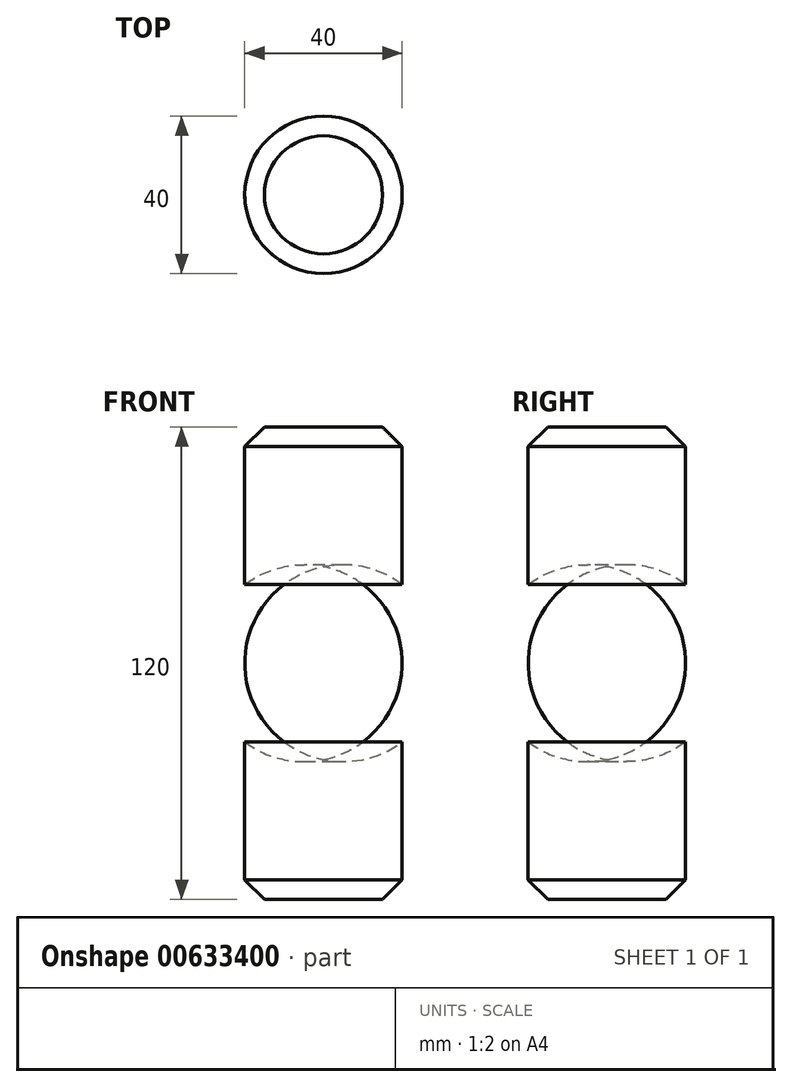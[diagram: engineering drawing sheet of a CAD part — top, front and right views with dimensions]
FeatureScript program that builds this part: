
annotation { "Feature Type Name" : "Feature", "Feature Type Description" : "" }
export const myFeature = defineFeature(function(context is Context, id is Id, definition is map)
    precondition{}
    {
        {
            var Q0;
            Q0=qCreatedBy(makeId("Front.planeOp"),FACE);
            var sketch = newSketch(context, id + "F0", { "sketchPlane" : qUnion([Q0])});
            skLineSegment(sketch, "E0", {"start": v(0, 60) * mm, "end": v(0, -60) * mm});
            skLineSegment(sketch, "E1", {"start": v(0, -60) * mm, "end": v(20, -60) * mm});
            skLineSegment(sketch, "E2", {"start": v(20, -60) * mm, "end": v(20, -20) * mm});
            skLineSegment(sketch, "E3", {"start": v(0, 60) * mm, "end": v(20, 60) * mm});
            skLineSegment(sketch, "E4", {"start": v(20, 60) * mm, "end": v(20, 20) * mm});
            skArc(sketch, "E5", {"start": v(20, -20) * mm, "mid": v(30, 0) * mm, "end": v(20, 20) * mm});
            skSolve(sketch);
        }
        {
            var Q0;
            Q0=makeQuery(id+"F0.imprint","IMPRINT",FACE,{"disambiguationData":[TD([[makeQuery(id+"F0.imprint","IMPRINT",EDGE,{"derivedFrom":sQuery(id+"F0.wireOp",EDGE,"E0")}),1.0]])]});
            var Q1;
            Q1=sQuery(id+"F0.wireOp",EDGE,"E0");
            revolve(context, id + "F1", {"entities" : qUnion([Q0]), "axis" : qUnion([Q1]), "revolveType" : RevolveType.FULL});
        }
        {
            var Q0;
            Q0=makeQuery(id+"F1.opRevolve","SWEPT_EDGE",EDGE,{"disambiguationData":[OSD([sQuery(id+"F0.wireOp",EDGE,"E3"),sQuery(id+"F0.wireOp",EDGE,"E4")])]});
            chamfer(context, id + "F2", {"entities" : qUnion([Q0]), "width" : 5 * mm, "tangentPropagation" : true});
        }
        {
            var Q0;
            Q0=makeQuery(id+"F1.opRevolve","SWEPT_EDGE",EDGE,{"disambiguationData":[OSD([sQuery(id+"F0.wireOp",EDGE,"E1"),sQuery(id+"F0.wireOp",EDGE,"E2")])]});
            chamfer(context, id + "F3", {"entities" : qUnion([Q0]), "width" : 5 * mm, "tangentPropagation" : true});
        }
        {
            var Q0;
            Q0=qCreatedBy(makeId("Front.planeOp"),FACE);
            cPlane(context, id + "F4", {"entities" : qUnion([Q0]), "cplaneType" : CPlaneType.OFFSET, "offset" : 25 * mm, "width" : 150 * mm, "height" : 150 * mm});
        }
        {
            var Q0;
            Q0=qCreatedBy(id+"F4.planeOp",FACE);
            var sketch = newSketch(context, id + "F5", { "sketchPlane" : qUnion([Q0])});
            skLineSegment(sketch, "E6.bottom", {"start": v(0, -10) * mm, "end": v(0, -10) * mm});
            skLineSegment(sketch, "E6.top", {"start": v(0, 10) * mm, "end": v(0, 10) * mm});
            skLineSegment(sketch, "E6.left", {"start": v(5, -5) * mm, "end": v(5, 5) * mm});
            skLineSegment(sketch, "E6.right", {"start": v(-5, -5) * mm, "end": v(-5, 5) * mm});
            skPoint(sketch, "E6.middle", {"position": v(0, 0) * mm});
            skPoint(sketch, "E7.visualSharp", {"position": v(-5, 10) * mm});
            skArc(sketch, "E7.filletArc", {"start": v(0, 10) * mm, "mid": v(-3.54, 8.54) * mm, "end": v(-5, 5) * mm});
            skPoint(sketch, "E8.visualSharp", {"position": v(5, 10) * mm});
            skArc(sketch, "E8.filletArc", {"start": v(5, 5) * mm, "mid": v(3.54, 8.54) * mm, "end": v(0, 10) * mm});
            skPoint(sketch, "E9.visualSharp", {"position": v(5, -10) * mm});
            skArc(sketch, "E9.filletArc", {"start": v(0, -10) * mm, "mid": v(3.54, -8.54) * mm, "end": v(5, -5) * mm});
            skPoint(sketch, "E10.visualSharp", {"position": v(-5, -10) * mm});
            skArc(sketch, "E10.filletArc", {"start": v(-5, -5) * mm, "mid": v(-3.54, -8.54) * mm, "end": v(0, -10) * mm});
            skSolve(sketch);
        }
        {
            var Q0;
            Q0=qCreatedBy(makeId("Right.planeOp"),FACE);
            var sketch = newSketch(context, id + "F6", { "sketchPlane" : qUnion([Q0])});
            skFitSpline(sketch, "E11", {"points": [v(-25, 0) * mm, v(-68.86, 35.46) * mm, v(-94.43, 26.77) * mm, v(-120.48, 33.53) * mm], "startDerivative": vector(-59.33, 123) * mm, "endDerivative": vector(-83.67, 41.82) * mm});
            skSolve(sketch);
        }
        {
            var Q0;
            Q0 = qSketchRegion(id + "F5", true);
            var Q1;
            Q1=sQuery(id+"F6.wireOp",EDGE,"E11");
            sweep(context, id + "F7", {"operationType" : NewBodyOperationType.ADD, "profiles" : qUnion([Q0]), "path" : qUnion([Q1])});
        }
        {
            var Q0;
            Q0=makeQuery(id+"F1.opRevolve","SWEPT_BODY",BODY,{"disambiguationData":[OSD([sQuery(id+"F0.wireOp",EDGE,"E0"),sQuery(id+"F0.wireOp",EDGE,"E1"),sQuery(id+"F0.wireOp",EDGE,"E2"),sQuery(id+"F0.wireOp",EDGE,"E3"),sQuery(id+"F0.wireOp",EDGE,"E4"),sQuery(id+"F0.wireOp",EDGE,"E5")])]});
            var Q1;
            Q1=makeQuery(id+"F1.opRevolve","SWEPT_FACE",FACE,{"disambiguationData":[OSD([sQuery(id+"F0.wireOp",EDGE,"E4")])]});
            circularPattern(context, id + "F8", {"entities" : qUnion([Q0]), "axis" : qUnion([Q1]), "angle" : 360 * degree, "instanceCount" : 5, "equalSpace" : true});
        }
        {
            var Q0;
            Q0=qCreatedBy(makeId("Front.planeOp"),FACE);
            var sketch = newSketch(context, id + "F9", { "sketchPlane" : qUnion([Q0])});
            skCircle(sketch, "E12", {"center": v(120, 30) * mm, "radius": 15 * mm});
            skSolve(sketch);
        }
        {
            var Q0;
            Q0 = qSketchRegion(id + "F9", true);
            var Q1;
            Q1=makeQuery(id+"F1.opRevolve","SWEPT_FACE",FACE,{"disambiguationData":[OSD([sQuery(id+"F0.wireOp",EDGE,"E4")])]});
            revolve(context, id + "F10", {"operationType" : NewBodyOperationType.ADD, "entities" : qUnion([Q0]), "axis" : qUnion([Q1]), "revolveType" : RevolveType.FULL});
        }
        {
            var Q0;
            Q0=makeQuery(id+"F10.boolean.opBoolean","INTERSECT",EDGE,{"derivedFrom":[makeQuery(id+"F8.opPattern","COPY",FACE,{"derivedFrom":makeQuery(id+"F7.opSweep","SWEPT_FACE",FACE,{"disambiguationData":[OSD([sQuery(id+"F5.wireOp",EDGE,"E6.left"),sQuery(id+"F6.wireOp",EDGE,"E11")])]}),"instanceName":"1"}),makeQuery(id+"F10.opRevolve","SWEPT_FACE",FACE,{"disambiguationData":[OSD([sQuery(id+"F9.wireOp",EDGE,"E12")])]})]});
            fillet(context, id + "F11", {"entities" : qUnion([Q0]), "radius" : 5 * mm, "tangentPropagation" : true, "allowEdgeOverflow" : false});
        }
        {
            var Q0;
            Q0=makeQuery(id+"F10.boolean.opBoolean","INTERSECT",EDGE,{"derivedFrom":[makeQuery(id+"F8.opPattern","COPY",FACE,{"derivedFrom":makeQuery(id+"F7.opSweep","SWEPT_FACE",FACE,{"disambiguationData":[OSD([sQuery(id+"F5.wireOp",EDGE,"E7.filletArc"),sQuery(id+"F5.wireOp",EDGE,"E8.filletArc"),sQuery(id+"F6.wireOp",EDGE,"E11")])]}),"instanceName":"2"}),makeQuery(id+"F10.opRevolve","SWEPT_FACE",FACE,{"disambiguationData":[OSD([sQuery(id+"F9.wireOp",EDGE,"E12")])]})]});
            var Q1;
            Q1=makeQuery(id+"F10.boolean.opBoolean","INTERSECT",EDGE,{"derivedFrom":[makeQuery(id+"F8.opPattern","COPY",FACE,{"derivedFrom":makeQuery(id+"F7.opSweep","SWEPT_FACE",FACE,{"disambiguationData":[OSD([sQuery(id+"F5.wireOp",EDGE,"E7.filletArc"),sQuery(id+"F5.wireOp",EDGE,"E8.filletArc"),sQuery(id+"F6.wireOp",EDGE,"E11")])]}),"instanceName":"3"}),makeQuery(id+"F10.opRevolve","SWEPT_FACE",FACE,{"disambiguationData":[OSD([sQuery(id+"F9.wireOp",EDGE,"E12")])]})]});
            fillet(context, id + "F12", {"entities" : qUnion([Q0, Q1]), "radius" : 5 * mm, "tangentPropagation" : true, "allowEdgeOverflow" : false});
        }
        {
            var Q0;
            Q0=makeQuery(id+"F10.boolean.opBoolean","INTERSECT",EDGE,{"derivedFrom":[makeQuery(id+"F7.opSweep","SWEPT_FACE",FACE,{"disambiguationData":[OSD([sQuery(id+"F5.wireOp",EDGE,"E7.filletArc"),sQuery(id+"F5.wireOp",EDGE,"E8.filletArc"),sQuery(id+"F6.wireOp",EDGE,"E11")])]}),makeQuery(id+"F10.opRevolve","SWEPT_FACE",FACE,{"disambiguationData":[OSD([sQuery(id+"F9.wireOp",EDGE,"E12")])]})]});
            var Q1;
            Q1=makeQuery(id+"F10.boolean.opBoolean","INTERSECT",EDGE,{"derivedFrom":[makeQuery(id+"F8.opPattern","COPY",FACE,{"derivedFrom":makeQuery(id+"F7.opSweep","SWEPT_FACE",FACE,{"disambiguationData":[OSD([sQuery(id+"F5.wireOp",EDGE,"E7.filletArc"),sQuery(id+"F5.wireOp",EDGE,"E8.filletArc"),sQuery(id+"F6.wireOp",EDGE,"E11")])]}),"instanceName":"4"}),makeQuery(id+"F10.opRevolve","SWEPT_FACE",FACE,{"disambiguationData":[OSD([sQuery(id+"F9.wireOp",EDGE,"E12")])]})]});
            fillet(context, id + "F13", {"entities" : qUnion([Q0, Q1]), "radius" : 5 * mm, "tangentPropagation" : true, "allowEdgeOverflow" : false});
        }
        {
            var Q0;
            {var subQ0=makeQuery(id+"F1.opRevolve","SWEPT_FACE",FACE,{"disambiguationData":[OSD([sQuery(id+"F0.wireOp",EDGE,"E5")])]});var subQ1=subQ0;Q0=makeQuery(id+"F10.boolean.opBoolean","INTERSECT",EDGE,{"disambiguationData":[topologyDisambiguationEdgeConnected([makeQuery(id+"F8.opPattern","COPY",FACE,{"derivedFrom":makeQuery(id+"F7.opSweep","SWEPT_FACE",FACE,{"disambiguationData":[OSD([sQuery(id+"F5.wireOp",EDGE,"E7.filletArc"),sQuery(id+"F5.wireOp",EDGE,"E8.filletArc"),sQuery(id+"F6.wireOp",EDGE,"E11")])]}),"instanceName":"2"})])],"derivedFrom":[subQ1,makeQuery(id+"F8.opPattern","COPY",FACE,{"derivedFrom":subQ1,"instanceName":"1"}),makeQuery(id+"F8.opPattern","COPY",FACE,{"derivedFrom":subQ1,"instanceName":"3"})]});}
            var Q1;
            {var subQ0=makeQuery(id+"F1.opRevolve","SWEPT_FACE",FACE,{"disambiguationData":[OSD([sQuery(id+"F0.wireOp",EDGE,"E5")])]});var subQ1=subQ0;Q1=makeQuery(id+"F10.boolean.opBoolean","INTERSECT",EDGE,{"disambiguationData":[topologyDisambiguationEdgeConnected([makeQuery(id+"F8.opPattern","COPY",FACE,{"derivedFrom":makeQuery(id+"F7.opSweep","SWEPT_FACE",FACE,{"disambiguationData":[OSD([sQuery(id+"F5.wireOp",EDGE,"E7.filletArc"),sQuery(id+"F5.wireOp",EDGE,"E8.filletArc"),sQuery(id+"F6.wireOp",EDGE,"E11")])]}),"instanceName":"3"})])],"derivedFrom":[subQ1,makeQuery(id+"F8.opPattern","COPY",FACE,{"derivedFrom":subQ1,"instanceName":"1"}),makeQuery(id+"F8.opPattern","COPY",FACE,{"derivedFrom":subQ1,"instanceName":"2"}),makeQuery(id+"F8.opPattern","COPY",FACE,{"derivedFrom":subQ1,"instanceName":"4"})]});}
            var Q2;
            {var subQ0=makeQuery(id+"F1.opRevolve","SWEPT_FACE",FACE,{"disambiguationData":[OSD([sQuery(id+"F0.wireOp",EDGE,"E5")])]});var subQ1=subQ0;Q2=makeQuery(id+"F10.boolean.opBoolean","INTERSECT",EDGE,{"disambiguationData":[topologyDisambiguationEdgeConnected([makeQuery(id+"F8.opPattern","COPY",FACE,{"derivedFrom":makeQuery(id+"F7.opSweep","SWEPT_FACE",FACE,{"disambiguationData":[OSD([sQuery(id+"F5.wireOp",EDGE,"E7.filletArc"),sQuery(id+"F5.wireOp",EDGE,"E8.filletArc"),sQuery(id+"F6.wireOp",EDGE,"E11")])]}),"instanceName":"4"})])],"derivedFrom":[subQ1,makeQuery(id+"F8.opPattern","COPY",FACE,{"derivedFrom":subQ1,"instanceName":"1"}),makeQuery(id+"F8.opPattern","COPY",FACE,{"derivedFrom":subQ1,"instanceName":"2"}),makeQuery(id+"F8.opPattern","COPY",FACE,{"derivedFrom":subQ1,"instanceName":"3"})]});}
            var Q3;
            Q3=makeQuery(id+"F7.boolean.opBoolean","INTERSECT",EDGE,{"derivedFrom":[makeQuery(id+"F1.opRevolve","SWEPT_FACE",FACE,{"disambiguationData":[OSD([sQuery(id+"F0.wireOp",EDGE,"E5")])]}),makeQuery(id+"F7.opSweep","SWEPT_FACE",FACE,{"disambiguationData":[OSD([sQuery(id+"F5.wireOp",EDGE,"E7.filletArc"),sQuery(id+"F5.wireOp",EDGE,"E8.filletArc"),sQuery(id+"F6.wireOp",EDGE,"E11")])]})]});
            var Q4;
            {var subQ0=makeQuery(id+"F1.opRevolve","SWEPT_FACE",FACE,{"disambiguationData":[OSD([sQuery(id+"F0.wireOp",EDGE,"E5")])]});var subQ1=subQ0;Q4=makeQuery(id+"F10.boolean.opBoolean","INTERSECT",EDGE,{"disambiguationData":[topologyDisambiguationEdgeConnected([makeQuery(id+"F8.opPattern","COPY",FACE,{"derivedFrom":makeQuery(id+"F7.opSweep","SWEPT_FACE",FACE,{"disambiguationData":[OSD([sQuery(id+"F5.wireOp",EDGE,"E7.filletArc"),sQuery(id+"F5.wireOp",EDGE,"E8.filletArc"),sQuery(id+"F6.wireOp",EDGE,"E11")])]}),"instanceName":"1"})])],"derivedFrom":[subQ1,makeQuery(id+"F8.opPattern","COPY",FACE,{"derivedFrom":subQ1,"instanceName":"2"})]});}
            fillet(context, id + "F14", {"entities" : qUnion([Q0, Q1, Q2, Q3, Q4]), "radius" : 5 * mm, "tangentPropagation" : true, "allowEdgeOverflow" : false});
        }
    });
